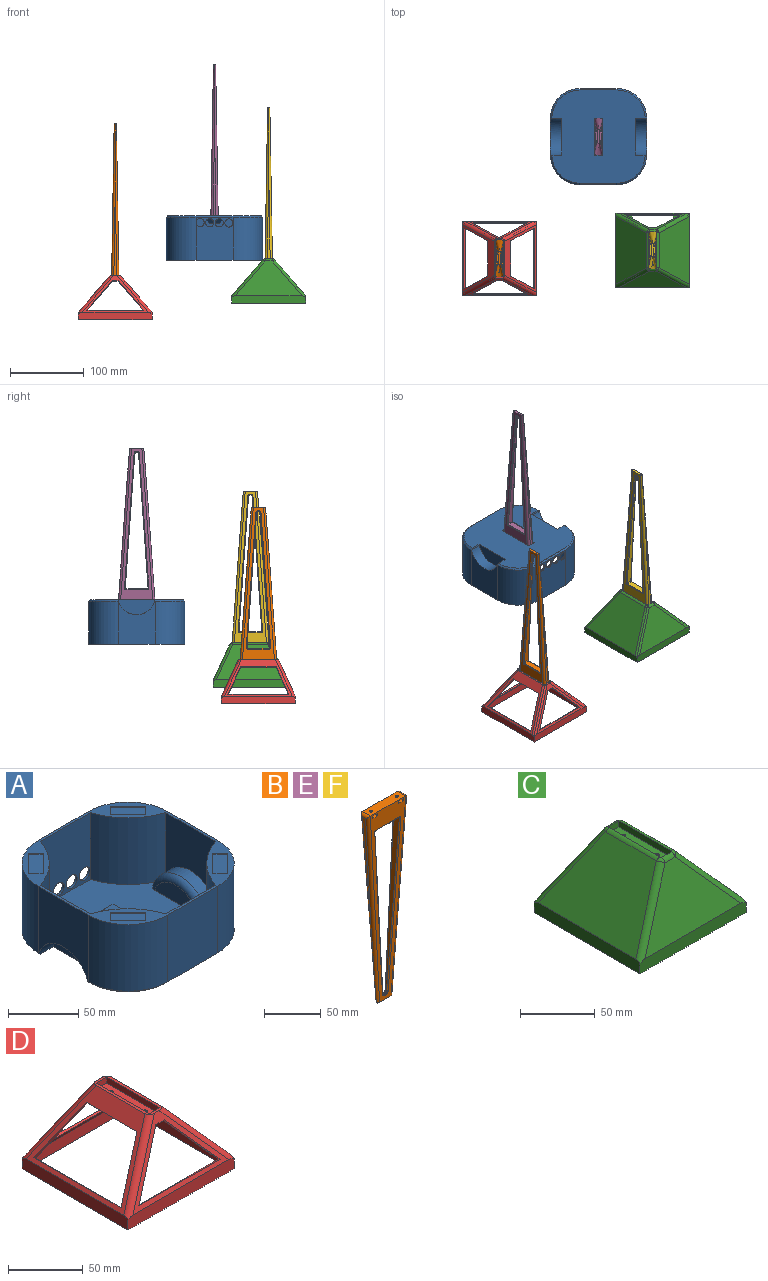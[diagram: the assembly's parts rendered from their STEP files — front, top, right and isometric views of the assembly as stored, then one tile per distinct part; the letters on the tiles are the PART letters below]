
ASSEMBLY  parts=6 mates=3
PART A: 79 faces, bbox 130x130x60.1 mm
  f0: plane 58x50mm, normal (1,0,0), area 2253.5mm2, adj f2,f5,f11,f59,f73,f76
  f1: plane 44x14mm, normal (0,0,1), area 559.5mm2, adj f26,f28,f67,f68,f69,f70
  f2: plane 130x130mm, normal (0,0,1), area 2459.1mm2, adj f0,f5,f6,f7,f8,f9,f10,f11
  f3: cylinder r=1.55mm len=3.1mm, axis (0,0,1), area 19.5mm2, adj f17,f29
  f4: cylinder r=1.55mm len=3.1mm, axis (0,0,1), area 19.5mm2, adj f17,f27
  f5: cylinder r=40mm len=58mm, axis (0,0,-1), area 3644.2mm2, adj f0,f2,f6,f73
  f6: plane 58x50mm, normal (0,1,0), area 2519.9mm2, adj f2,f5,f7,f51,f52,f53,f54,f75
  f7: cylinder r=40mm len=58mm, axis (0,0,-1), area 3644.2mm2, adj f2,f6,f8,f74
  f8: plane 58x50mm, normal (-1,0,0), area 2253.5mm2, adj f2,f7,f9,f65,f74,f77
  f9: cylinder r=40mm len=58mm, axis (0,0,-1), area 3644.2mm2, adj f2,f8,f10,f77
  f10: plane 58x50mm, normal (0,-1,0), area 2900mm2, adj f2,f9,f11,f78
  f11: cylinder r=40mm len=58mm, axis (0,0,-1), area 3644.2mm2, adj f0,f2,f10,f76
  f12: plane 126x126mm, normal (0,0,-1), area 12835.5mm2, adj f13,f14,f15,f16,f59,f60,f65,f66
  f13: plane 10x5mm, normal (0,1,0), area 50mm2, adj f12,f14,f16,f17
  f14: plane 50.1x5mm, normal (-1,0,0), area 250.5mm2, adj f12,f13,f15,f17
  f15: plane 10x5mm, normal (0,-1,0), area 50mm2, adj f12,f14,f16,f17
  f16: plane 50.1x5mm, normal (1,0,0), area 250.5mm2, adj f12,f13,f15,f17
  f17: plane 50.1x10mm, normal (0,0,-1), area 485.9mm2, adj f3,f4,f13,f14,f15,f16
  f18: plane 58x50mm, normal (0,-1,0), area 2519.9mm2, adj f2,f22,f25,f50,f51,f52,f53,f54
  f19: plane 53.87x50mm, normal (1,0,0), area 2124.1mm2, adj f2,f22,f23,f61
  f20: plane 58x50mm, normal (0,1,0), area 2900mm2, adj f2,f23,f24,f50
  f21: plane 53.87x50mm, normal (-1,0,0), area 2124.1mm2, adj f2,f24,f25,f55
  f22: cylinder r=60mm len=58mm, axis (0,0,1), area 3231.8mm2, adj f2,f18,f19,f50,f62
  f23: cylinder r=60mm len=58mm, axis (0,0,1), area 3231.8mm2, adj f2,f19,f20,f50,f63
  f24: cylinder r=60mm len=58mm, axis (0,0,1), area 3231.8mm2, adj f2,f20,f21,f50,f56
  f25: cylinder r=60mm len=58mm, axis (0,0,1), area 3231.8mm2, adj f2,f18,f21,f50,f57
  f26: cylinder r=3mm len=6mm, axis (0,0,1), area 56.5mm2, adj f1,f27
  f27: plane 6x6mm, normal (0,0,1), area 20.7mm2, adj f4,f26
  f28: cylinder r=3mm len=6mm, axis (0,0,1), area 56.5mm2, adj f1,f29
  f29: plane 6x6mm, normal (0,0,1), area 20.7mm2, adj f3,f28
  f30: plane 7.07x7.07mm, normal (-0.71,-0.71,0), area 10mm2, adj f2,f31,f33,f34
  f31: plane 17.68x17.68mm, normal (0.71,-0.71,0), area 25mm2, adj f2,f30,f32,f34
  f32: plane 7.07x7.07mm, normal (0.71,0.71,0), area 10mm2, adj f2,f31,f33,f34
  f33: plane 17.68x17.68mm, normal (-0.71,0.71,0), area 25mm2, adj f2,f30,f32,f34
  f34: plane 24.75x24.75mm, normal (0,0,1), area 250mm2, adj f30,f31,f32,f33
  f35: plane 7.07x7.07mm, normal (0.71,-0.71,0), area 10mm2, adj f2,f36,f38,f39
  f36: plane 17.68x17.68mm, normal (0.71,0.71,0), area 25mm2, adj f2,f35,f37,f39
  f37: plane 7.07x7.07mm, normal (-0.71,0.71,0), area 10mm2, adj f2,f36,f38,f39
  f38: plane 17.68x17.68mm, normal (-0.71,-0.71,0), area 25mm2, adj f2,f35,f37,f39
  f39: plane 24.75x24.75mm, normal (0,0,1), area 250mm2, adj f35,f36,f37,f38
  f40: plane 7.07x7.07mm, normal (-0.71,-0.71,0), area 10mm2, adj f2,f41,f43,f44
  f41: plane 17.68x17.68mm, normal (0.71,-0.71,0), area 25mm2, adj f2,f40,f42,f44
  f42: plane 7.07x7.07mm, normal (0.71,0.71,0), area 10mm2, adj f2,f41,f43,f44
  f43: plane 17.68x17.68mm, normal (-0.71,0.71,0), area 25mm2, adj f2,f40,f42,f44
  f44: plane 24.75x24.75mm, normal (0,0,1), area 250mm2, adj f40,f41,f42,f43
  f45: plane 7.07x7.07mm, normal (0.71,-0.71,0), area 10mm2, adj f2,f46,f48,f49
  f46: plane 17.68x17.68mm, normal (0.71,0.71,0), area 25mm2, adj f2,f45,f47,f49
  f47: plane 7.07x7.07mm, normal (-0.71,0.71,0), area 10mm2, adj f2,f46,f48,f49
  f48: plane 17.68x17.68mm, normal (-0.71,-0.71,0), area 25mm2, adj f2,f45,f47,f49
  f49: plane 24.75x24.75mm, normal (0,0,1), area 250mm2, adj f45,f46,f47,f48
  f50: plane 126x126mm, normal (0,0,1), area 8774.1mm2, adj f18,f20,f22,f23,f24,f25,f56,f57
  f51: cylinder r=5.5mm len=11mm, axis (0,1,0), area 69.1mm2, adj f6,f18
  f52: cylinder r=5.5mm len=11mm, axis (0,1,0), area 69.1mm2, adj f6,f18
  f53: cylinder r=5.5mm len=11mm, axis (0,1,0), area 69.1mm2, adj f6,f18
  f54: cylinder r=5.5mm len=11mm, axis (0,1,0), area 69.1mm2, adj f6,f18
  f55: cylinder r=27.62mm len=50mm, axis (1,0,0), area 625.1mm2, adj f21,f56,f57,f72
  f56: plane 13.56x4.13mm, normal (0,-1,0), area 51.8mm2, adj f24,f50,f55,f72
  f57: plane 13.56x4.13mm, normal (0,1,0), area 51.8mm2, adj f25,f50,f55,f72
  f58: plane 42.6x15mm, normal (-1,0,0), area 465.7mm2, adj f50,f72
  f59: cylinder r=25.62mm len=50mm, axis (1,0,0), area 1033.3mm2, adj f0,f12,f60,f73,f76
  f60: plane 50x20mm, normal (1,0,0), area 745.5mm2, adj f12,f59
  f61: cylinder r=27.62mm len=50mm, axis (-1,0,0), area 625.1mm2, adj f19,f62,f63,f71
  f62: plane 13.56x4.13mm, normal (0,1,0), area 51.8mm2, adj f22,f50,f61,f71
  f63: plane 13.56x4.13mm, normal (0,-1,0), area 51.8mm2, adj f23,f50,f61,f71
  f64: plane 42.6x15mm, normal (1,0,0), area 465.7mm2, adj f50,f71
  f65: cylinder r=25.62mm len=50mm, axis (-1,0,0), area 1033.3mm2, adj f8,f12,f66,f74,f77
  f66: plane 50x20mm, normal (-1,0,0), area 745.5mm2, adj f12,f65
  f67: plane 30x8mm, normal (0,-0.71,0.71), area 248.9mm2, adj f1,f50,f68,f69
  f68: plane 60x8mm, normal (-0.71,0,0.71), area 588.3mm2, adj f1,f50,f67,f70
  f69: plane 60x8mm, normal (0.71,0,0.71), area 588.3mm2, adj f1,f50,f67,f70
  f70: plane 30x8mm, normal (0,0.71,0.71), area 248.9mm2, adj f1,f50,f68,f69
  f71: torus R=22.62mm, axis (-1,0,0), area 491.4mm2, adj f50,f61,f62,f63,f64
  f72: torus R=22.62mm, axis (1,0,0), area 491.4mm2, adj f50,f55,f56,f57,f58
  f73: cone r=40mm half-angle=45deg, axis (0,0,1), area 174mm2, adj f0,f5,f12,f59,f75
  f74: cone r=40mm half-angle=45deg, axis (0,0,1), area 174mm2, adj f7,f8,f12,f65,f75
  f75: plane 50x2mm, normal (0,0.71,-0.71), area 141.4mm2, adj f6,f12,f73,f74
  f76: cone r=40mm half-angle=45deg, axis (0,0,1), area 174mm2, adj f0,f11,f12,f59,f78
  f77: cone r=40mm half-angle=45deg, axis (0,0,1), area 174mm2, adj f8,f9,f12,f65,f78
  f78: plane 50x2mm, normal (0,-0.71,-0.71), area 141.4mm2, adj f10,f12,f76,f77
PART B: 52 faces, bbox 50x10x210.2 mm
  f0: plane 210x43.99mm, normal (0,-1,-0.02), area 2341.6mm2, adj f3,f4,f8,f9,f10,f11,f13,f14
  f1: cylinder r=1.5mm len=3mm, axis (0,0,1), area 13.4mm2, adj f3,f13
  f2: cylinder r=1.5mm len=3mm, axis (0,0,1), area 14.1mm2, adj f3,f8
  f3: plane 43.56x10mm, normal (0,0,1), area 421.4mm2, adj f0,f1,f2,f7,f22,f25
  f4: plane 19.2x3mm, normal (0,0,-1), area 53.1mm2, adj f0,f7,f23,f24,f26,f27
  f5: plane 116.98x8.36mm, normal (1,0,-0.07), area 228.6mm2, adj f25,f26,f27
  f6: plane 116.98x8.36mm, normal (-1,0,-0.07), area 228.6mm2, adj f22,f23,f24
  f7: plane 210x43.99mm, normal (0,1,-0.02), area 2373.7mm2, adj f3,f4,f22,f24,f25,f26,f34,f35
  f8: plane 8.01x6.01mm, normal (0,0.02,-1), area 40.9mm2, adj f0,f2,f10,f11,f12
  f9: plane 8.01x6.01mm, normal (0,-0.02,1), area 40.9mm2, adj f0,f10,f11,f12,f19
  f10: plane 8.04x2.63mm, normal (1,0,0), area 20mm2, adj f0,f8,f9,f12
  f11: plane 8.04x2.63mm, normal (-1,0,0), area 20mm2, adj f0,f8,f9,f12
  f12: plane 6x2.5mm, normal (0,-1,-0.02), area 15mm2, adj f8,f9,f10,f11
  f13: plane 8.01x6.01mm, normal (0,0.02,-1), area 40.9mm2, adj f0,f1,f15,f16,f17
  f14: plane 8.01x6.01mm, normal (0,-0.02,1), area 40.9mm2, adj f0,f15,f16,f17,f21
  f15: plane 8.04x2.63mm, normal (1,0,0), area 20mm2, adj f0,f13,f14,f17
  f16: plane 8.04x2.63mm, normal (-1,0,0), area 20mm2, adj f0,f13,f14,f17
  f17: plane 6x2.5mm, normal (0,-1,-0.02), area 15mm2, adj f13,f14,f15,f16
  f18: plane 3x3mm, normal (0,0,1), area 7.1mm2, adj f19
  f19: cylinder r=1.5mm len=6.02mm, axis (0,0,1), area 56.5mm2, adj f9,f18
  f20: plane 3x3mm, normal (0,0,1), area 7.1mm2, adj f21
  f21: cylinder r=1.5mm len=6.11mm, axis (0,0,1), area 57.3mm2, adj f14,f20
  f22: cylinder r=3mm len=10mm, axis (0,-1,0), area 38.8mm2, adj f0,f3,f6,f7,f23,f24
  f23: cylinder r=3mm len=210.16mm, axis (-0.07,-0.02,1), area 916.8mm2, adj f0,f4,f6,f22,f24
  f24: cylinder r=3mm len=210.16mm, axis (0.07,-0.02,-1), area 916.8mm2, adj f4,f6,f7,f22,f23
  f25: cylinder r=3mm len=10mm, axis (0,-1,0), area 38.8mm2, adj f0,f3,f5,f7,f26,f27
  f26: cylinder r=3mm len=210.16mm, axis (0.07,0.02,1), area 916.8mm2, adj f4,f5,f7,f25,f27
  f27: cylinder r=3mm len=210.16mm, axis (-0.07,0.02,-1), area 916.8mm2, adj f0,f4,f5,f25,f26
  f28: plane 181.73x12.97mm, normal (-1,0,0.07), area 777.7mm2, adj f29,f39,f44,f49
  f29: cylinder r=2.5mm len=2.49mm, axis (0,1,-0.02), area 4.4mm2, adj f28,f30,f37,f51
  f30: plane 1.13x0.03mm, normal (0,0.02,1), area 0mm2, adj f29,f32,f35,f50
  f31: plane 28.96x7.37mm, normal (0,-0.02,-1), area 213.5mm2, adj f40,f41,f44,f45
  f32: cylinder r=2.5mm len=2.49mm, axis (0,1,-0.02), area 4.4mm2, adj f30,f33,f34,f48
  f33: plane 181.73x12.97mm, normal (1,0,0.07), area 777.7mm2, adj f32,f36,f41,f46
  f34: torus R=3.5mm, axis (0,-1,0.02), area 6.7mm2, adj f7,f32,f35,f36
  f35: cylinder r=1mm len=1.02mm, axis (-1,0,0), area 0mm2, adj f7,f30,f34,f37
  f36: cylinder r=1mm len=181.7mm, axis (-0.07,0.02,1), area 286mm2, adj f7,f33,f34,f38
  f37: torus R=3.5mm, axis (0,-1,0.02), area 6.7mm2, adj f7,f29,f35,f39
  f38: torus R=2mm, axis (0,-1,0.02), area 3.5mm2, adj f7,f36,f40,f41
  f39: cylinder r=1mm len=181.7mm, axis (-0.07,-0.02,-1), area 286mm2, adj f7,f28,f37,f42
  f40: cylinder r=1mm len=28.96mm, axis (1,0,0), area 45.5mm2, adj f7,f31,f38,f42
  f41: cylinder r=1mm len=7.39mm, axis (0,1,-0.02), area 12.1mm2, adj f31,f33,f38,f43
  f42: torus R=2mm, axis (0,-1,0.02), area 3.5mm2, adj f7,f39,f40,f44
  f43: bspline ~2.35x2.35mm, area 3.5mm2, adj f0,f41,f45,f46
  f44: cylinder r=1mm len=7.39mm, axis (0,1,-0.02), area 12.1mm2, adj f28,f31,f42,f47
  f45: cylinder r=1mm len=28.96mm, axis (-1,0,0), area 44.5mm2, adj f0,f31,f43,f47
  f46: cylinder r=1mm len=181.8mm, axis (0.07,0.02,-1), area 286.6mm2, adj f0,f33,f43,f48
  f47: bspline ~2.35x2.35mm, area 3.5mm2, adj f0,f44,f45,f49
  f48: bspline ~3.65x3.5mm, area 6.8mm2, adj f0,f32,f46,f50
  f49: cylinder r=1mm len=181.8mm, axis (0.07,-0.02,1), area 286.6mm2, adj f0,f28,f47,f51
  f50: cylinder r=1mm len=1.02mm, axis (1,0,0), area 0mm2, adj f0,f30,f48,f51
  f51: bspline ~3.65x3.5mm, area 6.8mm2, adj f0,f29,f49,f50
PART C: 85 faces, bbox 103.3x102.8x60 mm
  f0: plane 100x100mm, normal (0,0,-1), area 1360mm2, adj f1,f2,f5,f6,f7,f8,f13,f14
  f1: plane 96x9.26mm, normal (1,0,0), area 688.8mm2, adj f0,f2,f14,f18,f41,f43,f50,f52
  f2: plane 96x9.56mm, normal (0,1,0), area 717.9mm2, adj f0,f1,f13,f16,f17,f18,f42,f43
  f3: cylinder r=1.55mm len=3.1mm, axis (0,0,-1), area 9.7mm2, adj f28,f32
  f4: cylinder r=1.55mm len=3.1mm, axis (0,0,-1), area 9.7mm2, adj f28,f30
  f5: plane 100x10mm, normal (0,-1,0), area 993.2mm2, adj f0,f6,f8,f10,f37,f38
  f6: plane 100x10mm, normal (1,0,0), area 994.8mm2, adj f0,f5,f7,f11,f37,f39
  f7: plane 100x10mm, normal (0,1,0), area 993.2mm2, adj f0,f6,f8,f9,f39,f40
  f8: plane 100x10mm, normal (-1,0,0), area 994.8mm2, adj f0,f5,f7,f12,f38,f40
  f9: plane 90.4x47.09mm, normal (0,0.91,0.42), area 741mm2, adj f7,f39,f40,f57,f81,f82,f83,f84
  f10: plane 90.4x47.09mm, normal (0,-0.91,0.42), area 2586.8mm2, adj f5,f37,f38,f56
  f11: plane 91.99x48.26mm, normal (0.76,0,0.65), area 4442.4mm2, adj f6,f37,f39,f60
  f12: plane 91.99x48.26mm, normal (-0.76,0,0.65), area 4442.4mm2, adj f8,f38,f40,f53
  f13: plane 96x9.26mm, normal (-1,0,0), area 688.8mm2, adj f0,f2,f14,f17,f44,f46,f47,f49
  f14: plane 96x9.56mm, normal (0,-1,0), area 717.9mm2, adj f0,f1,f13,f15,f17,f18,f48,f49
  f15: plane 95.48x48.44mm, normal (0,-0.91,-0.42), area 1023.8mm2, adj f14,f17,f18,f21,f81,f82,f83,f84
  f16: plane 95.48x48.44mm, normal (0,0.91,-0.42), area 2869.6mm2, adj f2,f17,f18,f19
  f17: plane 96x48.74mm, normal (-0.76,0,-0.65), area 4748.1mm2, adj f2,f13,f14,f15,f16,f22
  f18: plane 96x48.74mm, normal (0.76,0,-0.65), area 4748.1mm2, adj f1,f2,f14,f15,f16,f20
  f19: plane 12.16x3mm, normal (0,-1,0), area 36.5mm2, adj f16,f20,f22,f36
  f20: plane 51.44x3mm, normal (-1,0,0), area 154.3mm2, adj f18,f19,f21,f34
  f21: plane 12.16x3mm, normal (0,1,0), area 36.5mm2, adj f15,f20,f22,f33
  f22: plane 51.44x3mm, normal (1,0,0), area 154.3mm2, adj f17,f19,f21,f35
  f23: plane 47.44x8.16mm, normal (0,0,-1), area 330.7mm2, adj f29,f31,f33,f34,f35,f36
  f24: plane 10.1x4.84mm, normal (0,1,0), area 48.9mm2, adj f25,f27,f28,f54,f56,f58
  f25: plane 50.1x4.99mm, normal (-1,0,0), area 249.8mm2, adj f24,f26,f28,f58,f59,f60
  f26: plane 10.1x4.84mm, normal (0,-1,0), area 48.9mm2, adj f25,f27,f28,f55,f57,f59
  f27: plane 50.1x4.99mm, normal (1,0,0), area 249.8mm2, adj f24,f26,f28,f53,f54,f55
  f28: plane 50.1x10.1mm, normal (0,0,1), area 490.9mm2, adj f3,f4,f24,f25,f26,f27
  f29: cylinder r=3mm len=6mm, axis (0,0,-1), area 18.8mm2, adj f23,f30
  f30: plane 6x6mm, normal (0,0,-1), area 20.7mm2, adj f4,f29
  f31: cylinder r=3mm len=6mm, axis (0,0,-1), area 18.8mm2, adj f23,f32
  f32: plane 6x6mm, normal (0,0,-1), area 20.7mm2, adj f3,f31
  f33: plane 12.16x2mm, normal (0,0.71,-0.71), area 28.7mm2, adj f21,f23,f34,f35
  f34: plane 51.44x2mm, normal (-0.71,0,-0.71), area 139.8mm2, adj f20,f23,f33,f36
  f35: plane 51.44x2mm, normal (0.71,0,-0.71), area 139.8mm2, adj f22,f23,f33,f36
  f36: plane 12.16x2mm, normal (0,-0.71,-0.71), area 28.7mm2, adj f19,f23,f34,f35
  f37: cylinder r=5mm len=51.59mm, axis (0.62,-0.33,-0.72), area 441mm2, adj f5,f6,f10,f11,f58
  f38: cylinder r=5mm len=51.59mm, axis (-0.62,-0.33,-0.72), area 441mm2, adj f5,f8,f10,f12,f54
  f39: cylinder r=5mm len=51.59mm, axis (0.62,0.33,-0.72), area 441mm2, adj f6,f7,f9,f11,f59
  f40: cylinder r=5mm len=51.59mm, axis (-0.62,0.33,-0.72), area 441mm2, adj f7,f8,f9,f12,f55
  f41: plane 20x5mm, normal (0,1,0), area 100mm2, adj f0,f1,f42,f43
  f42: plane 20x5mm, normal (1,0,0), area 100mm2, adj f0,f2,f41,f43
  f43: plane 20x20mm, normal (0,0,1), area 400mm2, adj f1,f2,f41,f42
  f44: plane 20x5mm, normal (0,1,0), area 100mm2, adj f0,f13,f45,f46
  f45: plane 20x5mm, normal (-1,0,0), area 100mm2, adj f0,f2,f44,f46
  f46: plane 20x20mm, normal (0,0,1), area 400mm2, adj f2,f13,f44,f45
  f47: plane 20x5mm, normal (0,-1,0), area 100mm2, adj f0,f13,f48,f49
  f48: plane 20x5mm, normal (-1,0,0), area 100mm2, adj f0,f14,f47,f49
  f49: plane 20x20mm, normal (0,0,1), area 400mm2, adj f13,f14,f47,f48
  f50: plane 20x5mm, normal (0,-1,0), area 100mm2, adj f0,f1,f51,f52
  f51: plane 20x5mm, normal (1,0,0), area 100mm2, adj f0,f14,f50,f52
  f52: plane 20x20mm, normal (0,0,1), area 400mm2, adj f1,f14,f50,f51
  f53: cylinder r=5mm len=47.59mm, axis (0,1,0), area 188.4mm2, adj f12,f27,f54,f55
  f54: sphere r=5mm, area 13.9mm2, adj f24,f27,f38,f53,f56
  f55: sphere r=5mm, area 13.9mm2, adj f26,f27,f40,f53,f57
  f56: cylinder r=5mm len=9.41mm, axis (-1,0,0), area 41.7mm2, adj f10,f24,f54,f58
  f57: cylinder r=5mm len=9.41mm, axis (-1,0,0), area 41.7mm2, adj f9,f26,f55,f59
  f58: sphere r=5mm, area 13.9mm2, adj f24,f25,f37,f56,f60
  f59: sphere r=5mm, area 13.9mm2, adj f25,f26,f39,f57,f60
  f60: cylinder r=5mm len=47.59mm, axis (0,1,0), area 188.4mm2, adj f11,f25,f58,f59
  f61: plane 16x2mm, normal (-1,0,0), area 32mm2, adj f0,f62,f64,f65
  f62: plane 16x2mm, normal (0,1,0), area 32mm2, adj f0,f61,f63,f65
  f63: plane 16x2mm, normal (1,0,0), area 32mm2, adj f0,f62,f64,f65
  f64: plane 16x2mm, normal (0,-1,0), area 32mm2, adj f0,f61,f63,f65
  f65: plane 16x16mm, normal (0,0,-1), area 256mm2, adj f61,f62,f63,f64
  f66: plane 16x2mm, normal (0,-1,0), area 32mm2, adj f0,f67,f69,f70
  f67: plane 16x2mm, normal (-1,0,0), area 32mm2, adj f0,f66,f68,f70
  f68: plane 16x2mm, normal (0,1,0), area 32mm2, adj f0,f67,f69,f70
  f69: plane 16x2mm, normal (1,0,0), area 32mm2, adj f0,f66,f68,f70
  f70: plane 16x16mm, normal (0,0,-1), area 256mm2, adj f66,f67,f68,f69
  f71: plane 16x2mm, normal (1,0,0), area 32mm2, adj f0,f72,f74,f75
  f72: plane 16x2mm, normal (0,-1,0), area 32mm2, adj f0,f71,f73,f75
  f73: plane 16x2mm, normal (-1,0,0), area 32mm2, adj f0,f72,f74,f75
  f74: plane 16x2mm, normal (0,1,0), area 32mm2, adj f0,f71,f73,f75
  f75: plane 16x16mm, normal (0,0,-1), area 256mm2, adj f71,f72,f73,f74
  f76: plane 16x2mm, normal (0,-1,0), area 32mm2, adj f0,f77,f79,f80
  f77: plane 16x2mm, normal (-1,0,0), area 32mm2, adj f0,f76,f78,f80
  f78: plane 16x2mm, normal (0,1,0), area 32mm2, adj f0,f77,f79,f80
  f79: plane 16x2mm, normal (1,0,0), area 32mm2, adj f0,f76,f78,f80
  f80: plane 16x16mm, normal (0,0,-1), area 256mm2, adj f76,f77,f78,f79
  f81: plane 40.16x33.82mm, normal (-0.79,0.26,-0.56), area 109.9mm2, adj f9,f15,f82,f83
  f82: plane 8.83x1.82mm, normal (0,0.42,-0.91), area 17.7mm2, adj f9,f15,f81,f84
  f83: plane 76.46x1.82mm, normal (0,-0.42,0.91), area 152.9mm2, adj f9,f15,f81,f84
  f84: plane 40.16x33.82mm, normal (0.79,0.26,-0.56), area 109.9mm2, adj f9,f15,f82,f83
PART D: 58 faces, bbox 103.3x102.8x61.4 mm
  f0: cylinder r=1.55mm len=3.1mm, axis (0,0,-1), area 9.7mm2, adj f29,f33
  f1: cylinder r=1.55mm len=3.1mm, axis (0,0,-1), area 9.7mm2, adj f29,f31
  f2: plane 54x14mm, normal (0,0,1), area 234.8mm2, adj f8,f9,f10,f11,f25,f26,f27,f28
  f3: plane 100x100mm, normal (0,0,-1), area 784mm2, adj f4,f5,f6,f7,f12,f13,f14,f15
  f4: plane 100x10mm, normal (0,-1,0), area 993.2mm2, adj f3,f5,f7,f9,f38,f39
  f5: plane 100x10mm, normal (1,0,0), area 994.8mm2, adj f3,f4,f6,f10,f38,f40
  f6: plane 100x10mm, normal (0,1,0), area 993.2mm2, adj f3,f5,f7,f8,f40,f41
  f7: plane 100x10mm, normal (-1,0,0), area 994.8mm2, adj f3,f4,f6,f11,f39,f41
  f8: plane 90.4x50mm, normal (0,0.91,0.42), area 738.6mm2, adj f2,f6,f40,f41,f42,f43,f44,f45
  f9: plane 90.4x50mm, normal (0,-0.91,0.42), area 757.5mm2, adj f2,f4,f38,f39,f50,f51,f52,f53
  f10: plane 91.99x50mm, normal (0.76,0,0.65), area 1322.4mm2, adj f2,f5,f38,f40,f54,f55,f56,f57
  f11: plane 91.99x50mm, normal (-0.76,0,0.65), area 1322.4mm2, adj f2,f7,f39,f41,f46,f47,f48,f49
  f12: plane 96x9.56mm, normal (0,1,0), area 917.9mm2, adj f3,f13,f15,f17,f18,f19
  f13: plane 96x9.26mm, normal (-1,0,0), area 888.8mm2, adj f3,f12,f14,f18
  f14: plane 96x9.56mm, normal (0,-1,0), area 917.9mm2, adj f3,f13,f15,f16,f18,f19
  f15: plane 96x9.26mm, normal (1,0,0), area 888.8mm2, adj f3,f12,f14,f19
  f16: plane 95.48x48.44mm, normal (0,-0.91,-0.42), area 999.2mm2, adj f14,f18,f19,f22,f42,f43,f44,f45
  f17: plane 95.48x48.44mm, normal (0,0.91,-0.42), area 1018.1mm2, adj f12,f18,f19,f20,f50,f51,f52,f53
  f18: plane 96x48.74mm, normal (-0.76,0,-0.65), area 1520.7mm2, adj f12,f13,f14,f16,f17,f23,f54,f55
  f19: plane 96x48.74mm, normal (0.76,0,-0.65), area 1520.7mm2, adj f12,f14,f15,f16,f17,f21,f46,f47
  f20: plane 12.16x3mm, normal (0,-1,0), area 36.5mm2, adj f17,f21,f23,f37
  f21: plane 51.44x3mm, normal (-1,0,0), area 154.3mm2, adj f19,f20,f22,f35
  f22: plane 12.16x3mm, normal (0,1,0), area 36.5mm2, adj f16,f21,f23,f34
  f23: plane 51.44x3mm, normal (1,0,0), area 154.3mm2, adj f18,f20,f22,f36
  f24: plane 47.44x8.16mm, normal (0,0,-1), area 330.7mm2, adj f30,f32,f34,f35,f36,f37
  f25: plane 10.1x5mm, normal (0,1,0), area 50.5mm2, adj f2,f26,f28,f29
  f26: plane 50.1x5mm, normal (-1,0,0), area 250.5mm2, adj f2,f25,f27,f29
  f27: plane 10.1x5mm, normal (0,-1,0), area 50.5mm2, adj f2,f26,f28,f29
  f28: plane 50.1x5mm, normal (1,0,0), area 250.5mm2, adj f2,f25,f27,f29
  f29: plane 50.1x10.1mm, normal (0,0,1), area 490.9mm2, adj f0,f1,f25,f26,f27,f28
  f30: cylinder r=3mm len=6mm, axis (0,0,-1), area 18.8mm2, adj f24,f31
  f31: plane 6x6mm, normal (0,0,-1), area 20.7mm2, adj f1,f30
  f32: cylinder r=3mm len=6mm, axis (0,0,-1), area 18.8mm2, adj f24,f33
  f33: plane 6x6mm, normal (0,0,-1), area 20.7mm2, adj f0,f32
  f34: plane 12.16x2mm, normal (0,0.71,-0.71), area 28.7mm2, adj f22,f24,f35,f36
  f35: plane 51.44x2mm, normal (-0.71,0,-0.71), area 139.8mm2, adj f21,f24,f34,f37
  f36: plane 51.44x2mm, normal (0.71,0,-0.71), area 139.8mm2, adj f23,f24,f34,f37
  f37: plane 12.16x2mm, normal (0,-0.71,-0.71), area 28.7mm2, adj f20,f24,f35,f36
  f38: cylinder r=5mm len=54.5mm, axis (0.62,-0.33,-0.72), area 458mm2, adj f2,f4,f5,f9,f10
  f39: cylinder r=5mm len=54.5mm, axis (-0.62,-0.33,-0.72), area 458mm2, adj f2,f4,f7,f9,f11
  f40: cylinder r=5mm len=54.5mm, axis (0.62,0.33,-0.72), area 458mm2, adj f2,f5,f6,f8,f10
  f41: cylinder r=5mm len=54.5mm, axis (-0.62,0.33,-0.72), area 458mm2, adj f2,f6,f7,f8,f11
  f42: plane 44.66x37.69mm, normal (-0.79,0.26,-0.56), area 122.4mm2, adj f8,f16,f43,f44
  f43: plane 76.46x1.82mm, normal (0,-0.42,0.91), area 152.9mm2, adj f8,f16,f42,f45
  f44: plane 1.82x1.09mm, normal (0,0.42,-0.91), area 2.2mm2, adj f8,f16,f42,f45
  f45: plane 44.66x37.69mm, normal (0.79,0.26,-0.56), area 122.4mm2, adj f8,f16,f43,f44
  f46: plane 38.87x33.82mm, normal (-0.21,-0.94,-0.25), area 104.9mm2, adj f11,f19,f47,f48
  f47: plane 82.42x1.52mm, normal (0.65,0,0.76), area 164.8mm2, adj f11,f19,f46,f49
  f48: plane 47.86x1.52mm, normal (-0.65,0,-0.76), area 95.7mm2, adj f11,f19,f46,f49
  f49: plane 38.87x33.82mm, normal (-0.21,0.94,-0.25), area 104.9mm2, adj f11,f19,f47,f48
  f50: plane 76.46x1.82mm, normal (0,0.42,0.91), area 152.9mm2, adj f9,f17,f51,f52
  f51: plane 40.78x34.35mm, normal (0.79,-0.26,-0.56), area 111.6mm2, adj f9,f17,f50,f53
  f52: plane 40.78x34.35mm, normal (-0.79,-0.26,-0.56), area 111.6mm2, adj f9,f17,f50,f53
  f53: plane 7.76x1.82mm, normal (0,-0.42,-0.91), area 15.5mm2, adj f9,f17,f51,f52
  f54: plane 82.42x1.52mm, normal (-0.65,0,0.76), area 164.8mm2, adj f10,f18,f55,f56
  f55: plane 38.87x33.82mm, normal (0.21,0.94,-0.25), area 104.9mm2, adj f10,f18,f54,f57
  f56: plane 38.87x33.82mm, normal (0.21,-0.94,-0.25), area 104.9mm2, adj f10,f18,f54,f57
  f57: plane 47.86x1.52mm, normal (0.65,0,-0.76), area 95.7mm2, adj f10,f18,f55,f56
PART E: same geometry as B
PART F: same geometry as B
PLACE A rot(axis=(-1,0,0),180deg) t=(127.99,181.48,55.03)mm
PLACE B rot(axis=(-0.71,-0.71,0),180deg) t=(-6.19,16.92,96.86)mm
PLACE C t=(201.26,27.78,-63.01)mm
PLACE D t=(-6.19,16.92,-85.41)mm
PLACE E rot(axis=(-0.71,-0.71,0),180deg) t=(127.99,181.48,177.3)mm
PLACE F rot(axis=(-0.71,-0.71,0),180deg) t=(201.26,27.78,119.26)mm
MATE fastened B.f3 <-> D.f29  axis (0,0,-1) through (-6.19,16.92,-30.41)mm
MATE fastened F.f3 <-> C.f28  axis (0,0,-1) through (201.26,27.78,-8.01)mm
MATE fastened E.f3 <-> A.f17  axis (0,0,-1) through (127.99,181.48,50.03)mm
